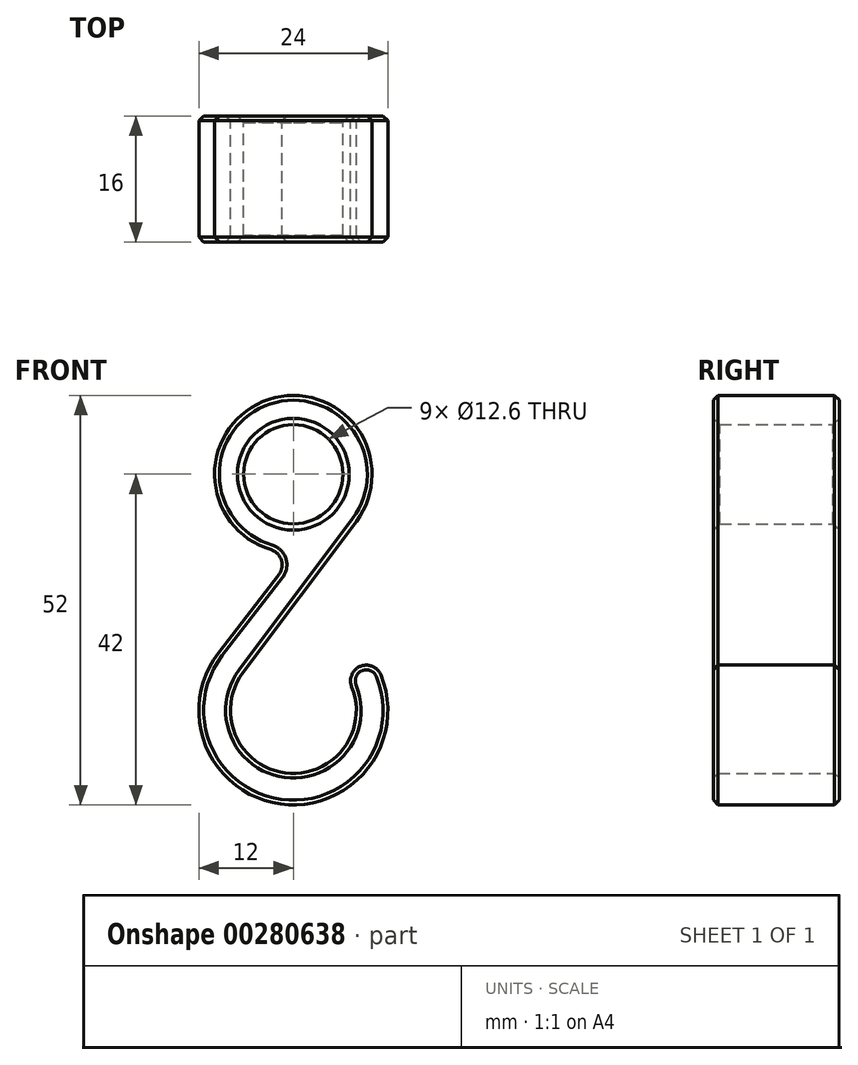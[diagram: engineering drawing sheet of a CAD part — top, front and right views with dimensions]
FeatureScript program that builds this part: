
annotation { "Feature Type Name" : "Feature", "Feature Type Description" : "" }
export const myFeature = defineFeature(function(context is Context, id is Id, definition is map)
    precondition{}
    {
        {
            var Q0;
            Q0=qCreatedBy(makeId("Front.planeOp"),FACE);
            var sketch = newSketch(context, id + "F0", { "sketchPlane" : qUnion([Q0])});
            skCircle(sketch, "E0", {"center": v(0, 0) * mm, "radius": 6.3 * mm});
            skCircle(sketch, "E1", {"center": v(0, -30) * mm, "radius": 8 * mm});
            skCircle(sketch, "E2", {"center": v(0, 0) * mm, "radius": 10 * mm});
            skCircle(sketch, "E3", {"center": v(0, -30) * mm, "radius": 12 * mm});
            skLineSegment(sketch, "E4", {"start": v(5, -3.84) * mm, "end": v(-9.5, -22.68) * mm});
            skLineSegment(sketch, "E5", {"start": v(8, -6) * mm, "end": v(-6.4, -25.2) * mm});
            skLineSegment(sketch, "E6", {"start": v(0, -30) * mm, "end": v(10, -23.37) * mm});
            skLineSegment(sketch, "E7", {"start": v(0, 0) * mm, "end": v(-9, -4.36) * mm});
            skSolve(sketch);
        }
        {
            var Q0;
            {var subQ0=sQuery(id+"F0.wireOp",EDGE,"E4");var subQ1=sQuery(id+"F0.wireOp",EDGE,"E0");var subQ2=makeQuery(id+"F0.imprint","INTERSECT",VERTEX,{"derivedFrom":[subQ1,subQ0]});Q0=makeQuery(id+"F0.imprint","IMPRINT",FACE,{"disambiguationData":[TD([[makeQuery(id+"F0.imprint","IMPRINT",EDGE,{"disambiguationData":[TD([[subQ2,-1.0]])],"derivedFrom":subQ1}),-1.0]])]});}
            var Q1;
            {var subQ0=sQuery(id+"F0.wireOp",EDGE,"E5");var subQ1=sQuery(id+"F0.wireOp",EDGE,"E2");var subQ2=makeQuery(id+"F0.imprint","INTERSECT",VERTEX,{"derivedFrom":[subQ1,subQ0]});Q1=makeQuery(id+"F0.imprint","IMPRINT",FACE,{"disambiguationData":[TD([[makeQuery(id+"F0.imprint","IMPRINT",EDGE,{"disambiguationData":[TD([[subQ2,1.0]])],"derivedFrom":subQ1}),-1.0]])]});}
            var Q2;
            {var subQ0=sQuery(id+"F0.wireOp",EDGE,"E5");var subQ1=sQuery(id+"F0.wireOp",EDGE,"E1");var subQ2=makeQuery(id+"F0.imprint","INTERSECT",VERTEX,{"derivedFrom":[subQ1,subQ0]});Q2=makeQuery(id+"F0.imprint","IMPRINT",FACE,{"disambiguationData":[TD([[makeQuery(id+"F0.imprint","IMPRINT",EDGE,{"disambiguationData":[TD([[subQ2,-1.0]])],"derivedFrom":subQ1}),-1.0]])]});}
            var Q3;
            {var subQ0=sQuery(id+"F0.wireOp",EDGE,"E4");var subQ1=sQuery(id+"F0.wireOp",EDGE,"E0");var subQ2=makeQuery(id+"F0.imprint","INTERSECT",VERTEX,{"derivedFrom":[subQ1,subQ0]});Q3=makeQuery(id+"F0.imprint","IMPRINT",FACE,{"disambiguationData":[TD([[makeQuery(id+"F0.imprint","IMPRINT",EDGE,{"disambiguationData":[TD([[subQ2,1.0]])],"derivedFrom":subQ1}),-1.0]])]});}
            extrude(context, id + "F1", {"entities" : qUnion([Q0, Q1, Q2, Q3]), "depth" : 16 * mm});
        }
        {
            var Q0;
            Q0=makeQuery(id+"F1.opExtrude","SWEPT_EDGE",EDGE,{"disambiguationData":[OSD([sQuery(id+"F0.wireOp",EDGE,"E0"),sQuery(id+"F0.wireOp",EDGE,"E7")])]});
            var Q1;
            Q1=makeQuery(id+"F1.opExtrude","SWEPT_EDGE",EDGE,{"disambiguationData":[OSD([sQuery(id+"F0.wireOp",EDGE,"E2"),sQuery(id+"F0.wireOp",EDGE,"E7")])]});
            var Q2;
            Q2=makeQuery(id+"F1.opExtrude","SWEPT_EDGE",EDGE,{"disambiguationData":[OSD([sQuery(id+"F0.wireOp",EDGE,"E3"),sQuery(id+"F0.wireOp",EDGE,"E6")])]});
            var Q3;
            Q3=makeQuery(id+"F1.opExtrude","SWEPT_EDGE",EDGE,{"disambiguationData":[OSD([sQuery(id+"F0.wireOp",EDGE,"E1"),sQuery(id+"F0.wireOp",EDGE,"E6")])]});
            fillet(context, id + "F2", {"entities" : qUnion([Q0, Q1, Q2, Q3]), "radius" : 2 * mm, "tangentPropagation" : true, "allowEdgeOverflow" : false});
        }
        {
            var Q0;
            Q0=makeQuery(id+"F1.opExtrude","CAP_EDGE",EDGE,{"disambiguationData":[OSD([sQuery(id+"F0.wireOp",EDGE,"E0")])],"isStart":false});
            var Q1;
            Q1=makeQuery(id+"F1.opExtrude","CAP_EDGE",EDGE,{"disambiguationData":[OSD([sQuery(id+"F0.wireOp",EDGE,"E0")])],"isStart":true});
            chamfer(context, id + "F3", {"entities" : qUnion([Q0, Q1]), "width" : 0.8 * mm, "tangentPropagation" : true});
        }
        {
            var Q0;
            Q0=makeQuery(id+"F1.opExtrude","CAP_EDGE",EDGE,{"disambiguationData":[OSD([sQuery(id+"F0.wireOp",EDGE,"E2")])],"isStart":false});
            var Q1;
            Q1=makeQuery(id+"F1.opExtrude","CAP_EDGE",EDGE,{"disambiguationData":[OSD([sQuery(id+"F0.wireOp",EDGE,"E5")])],"isStart":true});
            chamfer(context, id + "F4", {"entities" : qUnion([Q0, Q1]), "width" : 0.6 * mm, "tangentPropagation" : true});
        }
    });
